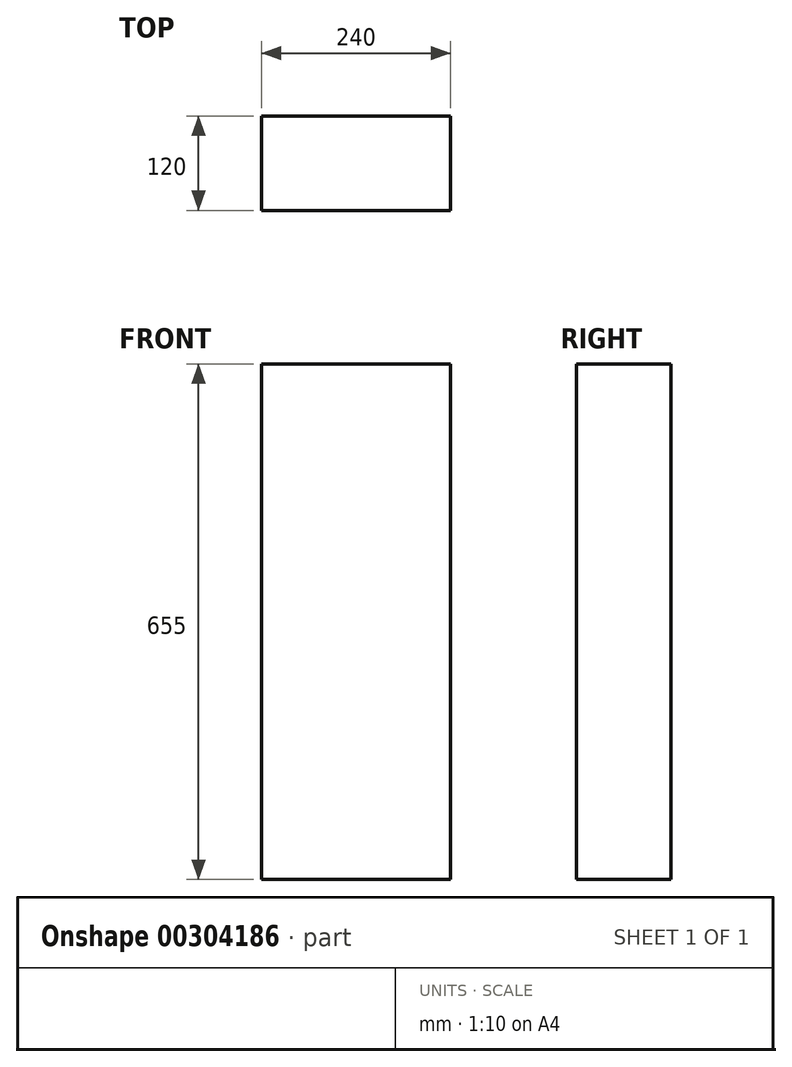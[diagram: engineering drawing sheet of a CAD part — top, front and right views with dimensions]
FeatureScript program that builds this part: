
annotation { "Feature Type Name" : "Feature", "Feature Type Description" : "" }
export const myFeature = defineFeature(function(context is Context, id is Id, definition is map)
    precondition{}
    {
        {
            var Q0;
            Q0=qCreatedBy(makeId("Top.planeOp"),FACE);
            var sketch = newSketch(context, id + "F0", { "sketchPlane" : qUnion([Q0])});
            skLineSegment(sketch, "E0.bottom", {"start": v(-99.8, -89.12) * mm, "end": v(140.2, -89.12) * mm});
            skLineSegment(sketch, "E0.top", {"start": v(-99.8, -209.12) * mm, "end": v(140.2, -209.12) * mm});
            skLineSegment(sketch, "E0.left", {"start": v(-99.8, -89.12) * mm, "end": v(-99.8, -209.12) * mm});
            skLineSegment(sketch, "E0.right", {"start": v(140.2, -89.12) * mm, "end": v(140.2, -209.12) * mm});
            skSolve(sketch);
        }
        {
            var Q0;
            Q0=makeQuery(id+"F0.imprint","IMPRINT",FACE,{"disambiguationData":[TD([[makeQuery(id+"F0.imprint","IMPRINT",EDGE,{"derivedFrom":sQuery(id+"F0.wireOp",EDGE,"E0.bottom")}),-1.0]])]});
            extrude(context, id + "F1", {"entities" : qUnion([Q0]), "depth" : 655 * mm});
        }
    });
